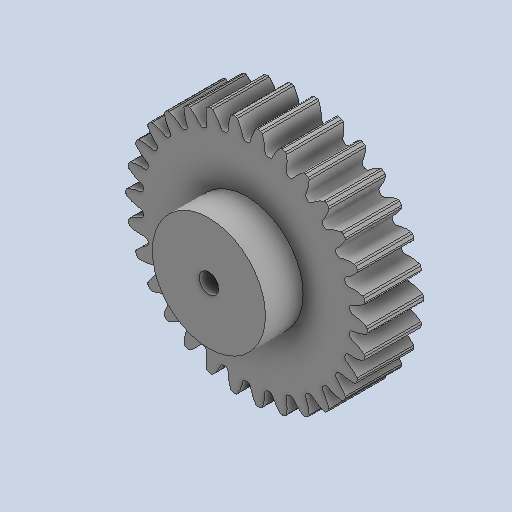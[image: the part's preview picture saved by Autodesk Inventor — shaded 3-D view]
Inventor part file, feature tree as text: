
AUTODESK INVENTOR PART (.ipt)
format: ipt  version: 2024 (Build 280153000, 153)  size: 764,928 bytes
history: native  units: mm
features: extrude x5, pattern_circular x2, sketch x1, fillet x1, other x1
ambient origin geometry x8: Origin, YZ Plane, XZ Plane, XY Plane, X Axis, Y Axis, Z Axis, Center Point
bodies: Solid1 (feature_tree)
feature tree (10):
  extrude  "Extrusion1"  TaperAngle=0.0deg  [1 undecoded]
  extrude  "Extrusion2"  Depth=300.0mm TaperAngle=360.0deg
  pattern_circular  "Circular Pattern1"  Count=3  [1 undecoded]
  sketch  "Sketch2"  dims[d0=15.0mm d1=0.0mm d2=0.0mm d3=0.0mm d4=300.0mm d5=360.0deg d7=30.0mm d8=5.2mm d9=10.0mm d10=0.0mm d11=0.5mm d12=300.0mm d13=360.0deg d15=0.0mm d16=0.0mm d19=0.0mm d20=0.0mm d14=0.0mm]
  extrude  "Extrusion3"  Depth=5.2mm
  fillet  "Fillet1"  Radius=10.0mm
  pattern_circular  "Circular Pattern2"  [2 undecoded]
  extrude  "Extrusion4"  Depth=300.0mm TaperAngle=360.0deg
  other  "Srf1"
  extrude  "ExtrusionSrf1"  TaperAngle=0.0deg  [1 undecoded]
note: 5 required parameter values undecoded (feature->parameter linkage not recoverable at this tier; creation-order binding heuristic only, values carry confidence <= 0.55)
